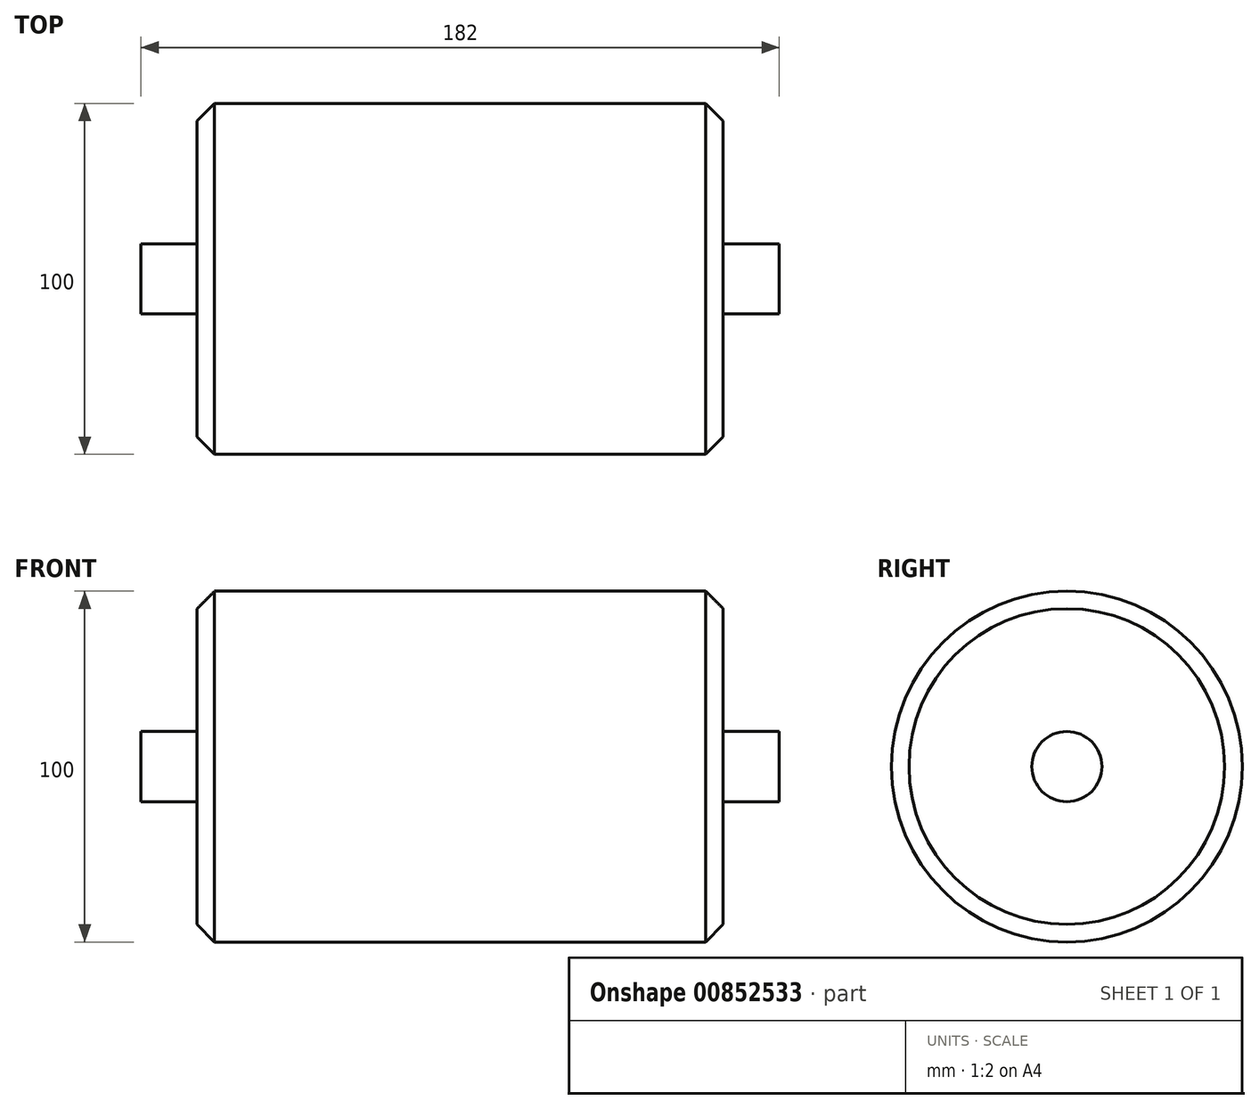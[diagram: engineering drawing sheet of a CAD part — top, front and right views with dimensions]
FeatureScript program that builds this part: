
annotation { "Feature Type Name" : "Feature", "Feature Type Description" : "" }
export const myFeature = defineFeature(function(context is Context, id is Id, definition is map)
    precondition{}
    {
        {
            var Q0;
            Q0=qCreatedBy(makeId("Front.planeOp"),FACE);
            var sketch = newSketch(context, id + "F0", { "sketchPlane" : qUnion([Q0])});
            skLineSegment(sketch, "E0", {"start": v(0, 50) * mm, "end": v(-75, 50) * mm});
            skLineSegment(sketch, "E1", {"start": v(-75, 50) * mm, "end": v(-75, 10) * mm});
            skLineSegment(sketch, "E2", {"start": v(-75, 10) * mm, "end": v(-91, 10) * mm});
            skLineSegment(sketch, "E3", {"start": v(-91, 10) * mm, "end": v(-91, 0) * mm});
            skLineSegment(sketch, "E4", {"start": v(-91, 0) * mm, "end": v(0, 0) * mm});
            skLineSegment(sketch, "E5.MirrorCS", {"start": v(0, 50) * mm, "end": v(75, 50) * mm});
            skLineSegment(sketch, "E6.MirrorCS", {"start": v(75, 50) * mm, "end": v(75, 10) * mm});
            skLineSegment(sketch, "E7.MirrorCS", {"start": v(91, 10) * mm, "end": v(91, 0) * mm});
            skLineSegment(sketch, "E8.MirrorCS", {"start": v(91, 0) * mm, "end": v(0, 0) * mm});
            skLineSegment(sketch, "E9.MirrorCS", {"start": v(75, 10) * mm, "end": v(91, 10) * mm});
            skSolve(sketch);
        }
        {
            var Q0;
            Q0=makeQuery(id+"F0.imprint","IMPRINT",FACE,{"disambiguationData":[TD([[makeQuery(id+"F0.imprint","IMPRINT",EDGE,{"derivedFrom":sQuery(id+"F0.wireOp",EDGE,"E0")}),1.0]])]});
            var Q1;
            Q1=sQuery(id+"F0.wireOp",EDGE,"E8.MirrorCS");
            revolve(context, id + "F1", {"surfaceOperationType" : NewSurfaceOperationType.NEW, "entities" : qUnion([Q0]), "axis" : qUnion([Q1]), "revolveType" : RevolveType.FULL});
        }
        {
            var Q0;
            Q0=makeQuery(id+"F1.opRevolve","SWEPT_EDGE",EDGE,{"disambiguationData":[OSD([sQuery(id+"F0.wireOp",EDGE,"E5.MirrorCS"),sQuery(id+"F0.wireOp",EDGE,"E6.MirrorCS")])]});
            var Q1;
            Q1=makeQuery(id+"F1.opRevolve","SWEPT_EDGE",EDGE,{"disambiguationData":[OSD([sQuery(id+"F0.wireOp",EDGE,"E0"),sQuery(id+"F0.wireOp",EDGE,"E1")])]});
            chamfer(context, id + "F2", {"entities" : qUnion([Q0, Q1]), "chamferType" : ChamferType.OFFSET_ANGLE, "width" : 5 * mm, "oppositeDirection" : false, "angle" : 45 * degree, "tangentPropagation" : true});
        }
    });
